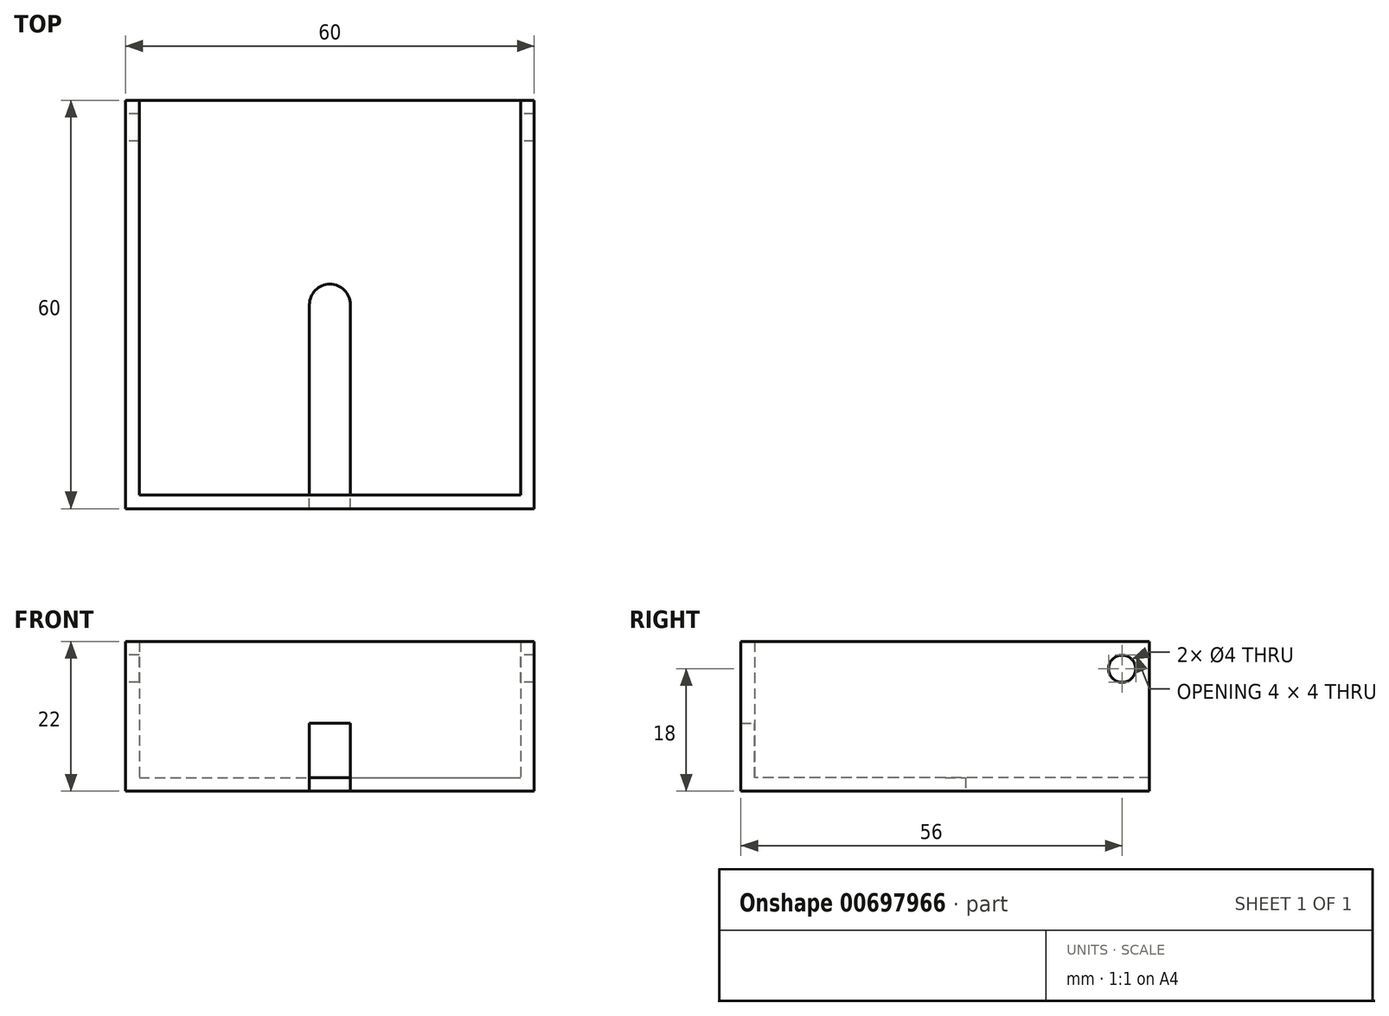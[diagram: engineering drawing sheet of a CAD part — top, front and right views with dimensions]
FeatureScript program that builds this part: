
annotation { "Feature Type Name" : "Feature", "Feature Type Description" : "" }
export const myFeature = defineFeature(function(context is Context, id is Id, definition is map)
    precondition{}
    {
        {
            var Q0;
            Q0=qCreatedBy(makeId("Top.planeOp"),FACE);
            var sketch = newSketch(context, id + "F0", { "sketchPlane" : qUnion([Q0])});
            skLineSegment(sketch, "E0.bottom", {"start": v(0, 0) * mm, "end": v(60, 0) * mm});
            skLineSegment(sketch, "E0.top", {"start": v(0, 60) * mm, "end": v(60, 60) * mm});
            skLineSegment(sketch, "E0.left", {"start": v(0, 0) * mm, "end": v(0, 60) * mm});
            skLineSegment(sketch, "E0.right", {"start": v(60, 0) * mm, "end": v(60, 60) * mm});
            skSolve(sketch);
        }
        {
            var Q0;
            Q0 = qSketchRegion(id + "F0", true);
            extrude(context, id + "F1", {"entities" : qUnion([Q0]), "depth" : 2 * mm, "offsetDistance" : 25 * mm});
        }
        {
            var Q0;
            Q0=makeQuery(id+"F1.opExtrude","CAP_FACE",FACE,{"disambiguationData":[OSD([sQuery(id+"F0.wireOp",EDGE,"E0.bottom"),sQuery(id+"F0.wireOp",EDGE,"E0.top"),sQuery(id+"F0.wireOp",EDGE,"E0.left"),sQuery(id+"F0.wireOp",EDGE,"E0.right")])],"isStart":false});
            var sketch = newSketch(context, id + "F2", { "sketchPlane" : qUnion([Q0])});
            skLineSegment(sketch, "E1.top", {"start": v(2, 2) * mm, "end": v(58, 2) * mm});
            skLineSegment(sketch, "E1.left", {"start": v(2, 60) * mm, "end": v(2, 2) * mm});
            skLineSegment(sketch, "E1.right", {"start": v(58, 60) * mm, "end": v(58, 2) * mm});
            skLineSegment(sketch, "E2.0.0", {"start": v(60, 60) * mm, "end": v(58, 60) * mm});
            skLineSegment(sketch, "E2.0.1", {"start": v(0, 60) * mm, "end": v(0, 0) * mm});
            skLineSegment(sketch, "E2.0.2", {"start": v(0, 0) * mm, "end": v(60, 0) * mm});
            skLineSegment(sketch, "E2.0.3", {"start": v(60, 0) * mm, "end": v(60, 60) * mm});
            skLineSegment(sketch, "E3.trimOffspring", {"start": v(2, 60) * mm, "end": v(0, 60) * mm});
            skSolve(sketch);
        }
        {
            var Q0;
            Q0 = qSketchRegion(id + "F2", true);
            extrude(context, id + "F3", {"entities" : qUnion([Q0]), "operationType" : NewBodyOperationType.ADD, "depth" : 20 * mm, "offsetDistance" : 25 * mm});
        }
        {
            var Q0;
            Q0=makeQuery(id+"F1.opExtrude","CAP_FACE",FACE,{"disambiguationData":[OSD([sQuery(id+"F0.wireOp",EDGE,"E0.bottom"),sQuery(id+"F0.wireOp",EDGE,"E0.top"),sQuery(id+"F0.wireOp",EDGE,"E0.left"),sQuery(id+"F0.wireOp",EDGE,"E0.right")])],"isStart":true});
            var sketch = newSketch(context, id + "F4", { "sketchPlane" : qUnion([Q0])});
            skLineSegment(sketch, "E4.bottom", {"start": v(27, 2.96) * mm, "end": v(33, 2.96) * mm});
            skLineSegment(sketch, "E4.left", {"start": v(27, 2.96) * mm, "end": v(27, -30) * mm});
            skLineSegment(sketch, "E4.right", {"start": v(33, 2.96) * mm, "end": v(33, -30) * mm});
            skArc(sketch, "E5", {"start": v(27, -30) * mm, "mid": v(30, -33) * mm, "end": v(33, -30) * mm});
            skSolve(sketch);
        }
        {
            var Q0;
            Q0 = qSketchRegion(id + "F4", true);
            extrude(context, id + "F5", {"entities" : qUnion([Q0]), "operationType" : NewBodyOperationType.REMOVE, "oppositeDirection" : true, "depth" : 10 * mm, "offsetDistance" : 25 * mm});
        }
        {
            var Q0;
            Q0=makeQuery(id+"F3.boolean.opBoolean","MERGE",FACE,{"derivedFrom":[makeQuery(id+"F1.opExtrude","SWEPT_FACE",FACE,{"disambiguationData":[OSD([sQuery(id+"F0.wireOp",EDGE,"E0.left")])]}),makeQuery(id+"F3.opExtrude","SWEPT_FACE",FACE,{"disambiguationData":[OSD([sQuery(id+"F2.wireOp",EDGE,"E2.0.1")])]})]});
            var sketch = newSketch(context, id + "F6", { "sketchPlane" : qUnion([Q0])});
            skCircle(sketch, "E6", {"center": v(-56, 18) * mm, "radius": 2 * mm});
            skSolve(sketch);
        }
        {
            var Q0;
            Q0 = qSketchRegion(id + "F6", true);
            extrude(context, id + "F7", {"entities" : qUnion([Q0]), "operationType" : NewBodyOperationType.REMOVE, "oppositeDirection" : true, "depth" : 69.4 * mm, "offsetDistance" : 25 * mm});
        }
    });
